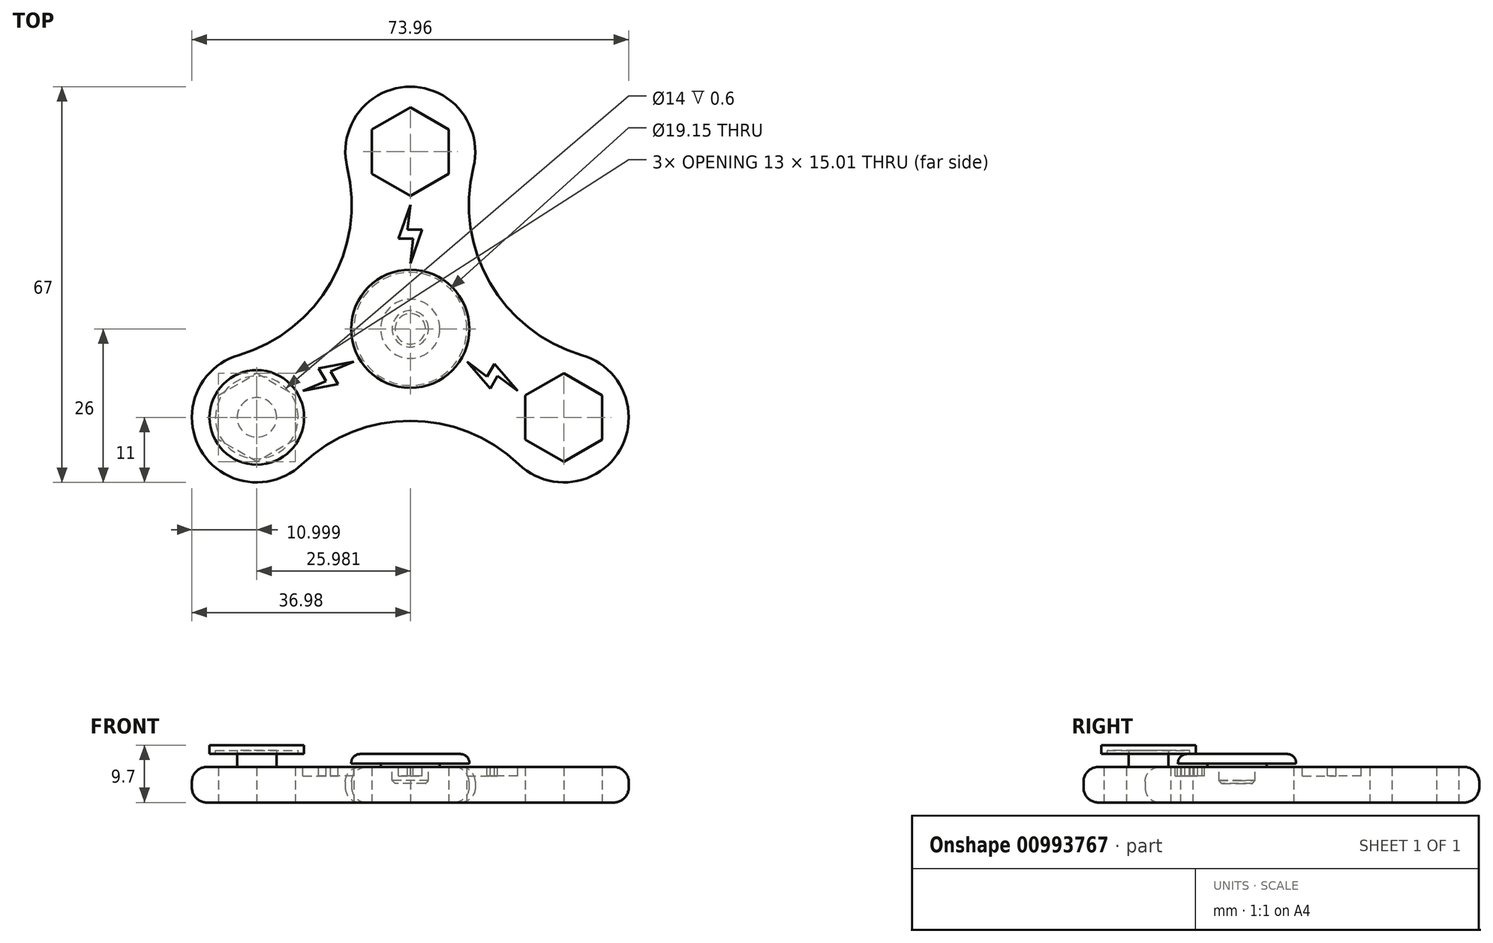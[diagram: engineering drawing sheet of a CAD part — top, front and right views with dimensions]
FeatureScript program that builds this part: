
annotation { "Feature Type Name" : "Feature", "Feature Type Description" : "" }
export const myFeature = defineFeature(function(context is Context, id is Id, definition is map)
    precondition{}
    {
        {
            var Q0;
            Q0=qCreatedBy(makeId("Top.planeOp"),FACE);
            var sketch = newSketch(context, id + "F0", { "sketchPlane" : qUnion([Q0])});
            skCircle(sketch, "E0", {"center": v(0, 0) * mm, "radius": 9.57 * mm});
            skLineSegment(sketch, "E1", {"start": v(0, 0) * mm, "end": v(0, 30) * mm, "construction": true});
            skLineSegment(sketch, "E2", {"start": v(0, 0) * mm, "end": v(25.98, -15) * mm, "construction": true});
            skLineSegment(sketch, "E3", {"start": v(0, 0) * mm, "end": v(-25.98, -15) * mm, "construction": true});
            skCircle(sketch, "E4", {"center": v(0, 0) * mm, "radius": 15.58 * mm, "construction": true});
            skArc(sketch, "E5", {"start": v(10.69, 27.39) * mm, "mid": v(0, 41) * mm, "end": v(-10.69, 27.39) * mm});
            skArc(sketch, "E6", {"start": v(18.38, -22.95) * mm, "mid": v(35.5, -20.5) * mm, "end": v(29.06, -4.44) * mm});
            skArc(sketch, "E7", {"start": v(-29.06, -4.44) * mm, "mid": v(-35.5, -20.5) * mm, "end": v(-18.38, -22.95) * mm});
            skArc(sketch, "E8", {"start": v(-29.06, -4.44) * mm, "mid": v(-13.49, 7.79) * mm, "end": v(-10.69, 27.39) * mm});
            skArc(sketch, "E9", {"start": v(10.69, 27.39) * mm, "mid": v(13.49, 7.79) * mm, "end": v(29.06, -4.44) * mm});
            skArc(sketch, "E10", {"start": v(18.38, -22.95) * mm, "mid": v(0, -15.57) * mm, "end": v(-18.38, -22.95) * mm});
            skCircle(sketch, "E11.cCircle", {"center": v(-25.98, -15) * mm, "radius": 6.5 * mm, "construction": true});
            skLineSegment(sketch, "E11.0", {"start": v(-19.48, -18.75) * mm, "end": v(-25.98, -22.5) * mm});
            skLineSegment(sketch, "E11.1", {"start": v(-25.98, -22.5) * mm, "end": v(-32.48, -18.75) * mm});
            skLineSegment(sketch, "E11.2", {"start": v(-32.48, -18.75) * mm, "end": v(-32.48, -11.25) * mm});
            skLineSegment(sketch, "E11.3", {"start": v(-32.48, -11.25) * mm, "end": v(-25.98, -7.5) * mm});
            skLineSegment(sketch, "E11.4", {"start": v(-25.98, -7.5) * mm, "end": v(-19.48, -11.25) * mm});
            skLineSegment(sketch, "E11.5", {"start": v(-19.48, -11.25) * mm, "end": v(-19.48, -18.75) * mm});
            skPoint(sketch, "E11.0.midPoint", {"position": v(-22.73, -20.63) * mm});
            skCircle(sketch, "E12.cCircle", {"center": v(25.98, -15) * mm, "radius": 6.5 * mm, "construction": true});
            skLineSegment(sketch, "E12.0", {"start": v(32.48, -18.75) * mm, "end": v(25.98, -22.5) * mm});
            skLineSegment(sketch, "E12.1", {"start": v(25.98, -22.5) * mm, "end": v(19.48, -18.75) * mm});
            skLineSegment(sketch, "E12.2", {"start": v(19.48, -18.75) * mm, "end": v(19.48, -11.25) * mm});
            skLineSegment(sketch, "E12.3", {"start": v(19.48, -11.25) * mm, "end": v(25.98, -7.5) * mm});
            skLineSegment(sketch, "E12.4", {"start": v(25.98, -7.5) * mm, "end": v(32.48, -11.25) * mm});
            skLineSegment(sketch, "E12.5", {"start": v(32.48, -11.25) * mm, "end": v(32.48, -18.75) * mm});
            skPoint(sketch, "E12.0.midPoint", {"position": v(29.23, -20.63) * mm});
            skCircle(sketch, "E13.cCircle", {"center": v(0, 30) * mm, "radius": 6.5 * mm, "construction": true});
            skLineSegment(sketch, "E13.0", {"start": v(-6.5, 33.75) * mm, "end": v(0, 37.5) * mm});
            skLineSegment(sketch, "E13.1", {"start": v(0, 37.5) * mm, "end": v(6.5, 33.75) * mm});
            skLineSegment(sketch, "E13.2", {"start": v(6.5, 33.75) * mm, "end": v(6.5, 26.25) * mm});
            skLineSegment(sketch, "E13.3", {"start": v(6.5, 26.25) * mm, "end": v(0, 22.5) * mm});
            skLineSegment(sketch, "E13.4", {"start": v(0, 22.5) * mm, "end": v(-6.5, 26.25) * mm});
            skLineSegment(sketch, "E13.5", {"start": v(-6.5, 26.25) * mm, "end": v(-6.5, 33.75) * mm});
            skPoint(sketch, "E13.0.midPoint", {"position": v(-3.25, 35.63) * mm});
            skSolve(sketch);
        }
        {
            var Q0;
            Q0 = qSketchRegion(id + "F0", true);
            extrude(context, id + "F1", {"entities" : qUnion([Q0]), "depth" : 6 * mm, "offsetDistance" : 25 * mm});
        }
        {
            var Q0;
            Q0=makeQuery(id+"F1.opExtrude","CAP_EDGE",EDGE,{"disambiguationData":[OSD([sQuery(id+"F0.wireOp",EDGE,"E8")])],"isStart":false});
            var Q1;
            Q1=makeQuery(id+"F1.opExtrude","CAP_EDGE",EDGE,{"disambiguationData":[OSD([sQuery(id+"F0.wireOp",EDGE,"E10")])],"isStart":true});
            fillet(context, id + "F2", {"entities" : qUnion([Q0, Q1]), "radius" : 2.5 * mm, "tangentPropagation" : true, "allowEdgeOverflow" : false});
        }
        {
            var Q0;
            Q0=makeQuery(id+"F1.opExtrude","CAP_FACE",FACE,{"disambiguationData":[OSD([sQuery(id+"F0.wireOp",EDGE,"E0"),sQuery(id+"F0.wireOp",EDGE,"E5"),sQuery(id+"F0.wireOp",EDGE,"E6"),sQuery(id+"F0.wireOp",EDGE,"E7"),sQuery(id+"F0.wireOp",EDGE,"E8"),sQuery(id+"F0.wireOp",EDGE,"E9"),sQuery(id+"F0.wireOp",EDGE,"E10"),sQuery(id+"F0.wireOp",EDGE,"E11.0"),sQuery(id+"F0.wireOp",EDGE,"E11.1"),sQuery(id+"F0.wireOp",EDGE,"E11.2"),sQuery(id+"F0.wireOp",EDGE,"E11.3"),sQuery(id+"F0.wireOp",EDGE,"E11.4"),sQuery(id+"F0.wireOp",EDGE,"E11.5"),sQuery(id+"F0.wireOp",EDGE,"E12.0"),sQuery(id+"F0.wireOp",EDGE,"E12.1"),sQuery(id+"F0.wireOp",EDGE,"E12.2"),sQuery(id+"F0.wireOp",EDGE,"E12.3"),sQuery(id+"F0.wireOp",EDGE,"E12.4"),sQuery(id+"F0.wireOp",EDGE,"E12.5"),sQuery(id+"F0.wireOp",EDGE,"E13.0"),sQuery(id+"F0.wireOp",EDGE,"E13.1"),sQuery(id+"F0.wireOp",EDGE,"E13.2"),sQuery(id+"F0.wireOp",EDGE,"E13.3"),sQuery(id+"F0.wireOp",EDGE,"E13.4"),sQuery(id+"F0.wireOp",EDGE,"E13.5")])],"isStart":false});
            var sketch = newSketch(context, id + "F3", { "sketchPlane" : qUnion([Q0])});
            skLineSegment(sketch, "E14", {"start": v(0, 21) * mm, "end": v(-2, 15.28) * mm});
            skLineSegment(sketch, "E15", {"start": v(0, 22.5) * mm, "end": v(0, 9.57) * mm, "construction": true});
            skLineSegment(sketch, "E16", {"start": v(-2, 15.28) * mm, "end": v(0.5, 15.28) * mm});
            skLineSegment(sketch, "E17", {"start": v(0, 11.07) * mm, "end": v(2, 16.78) * mm});
            skLineSegment(sketch, "E18", {"start": v(2, 16.78) * mm, "end": v(-0.5, 16.78) * mm});
            skLineSegment(sketch, "E19", {"start": v(0, 21) * mm, "end": v(-0.5, 16.78) * mm});
            skLineSegment(sketch, "E20", {"start": v(0, 11.07) * mm, "end": v(0.5, 15.28) * mm});
            skLineSegment(sketch, "E21.1.0", {"start": v(-18.18, -10.5) * mm, "end": v(-12.24, -9.37) * mm});
            skLineSegment(sketch, "E21.1.1", {"start": v(-18.18, -10.5) * mm, "end": v(-14.29, -8.83) * mm});
            skLineSegment(sketch, "E21.1.2", {"start": v(-15.54, -6.66) * mm, "end": v(-14.29, -8.83) * mm});
            skLineSegment(sketch, "E21.1.3", {"start": v(-9.6, -5.54) * mm, "end": v(-15.54, -6.66) * mm});
            skLineSegment(sketch, "E21.1.4", {"start": v(-9.6, -5.54) * mm, "end": v(-13.49, -7.2) * mm});
            skLineSegment(sketch, "E21.1.5", {"start": v(-12.24, -9.37) * mm, "end": v(-13.49, -7.2) * mm});
            skLineSegment(sketch, "E21.2.0", {"start": v(18.18, -10.5) * mm, "end": v(14.24, -5.91) * mm});
            skLineSegment(sketch, "E21.2.1", {"start": v(18.18, -10.5) * mm, "end": v(14.79, -7.96) * mm});
            skLineSegment(sketch, "E21.2.2", {"start": v(13.54, -10.12) * mm, "end": v(14.79, -7.96) * mm});
            skLineSegment(sketch, "E21.2.3", {"start": v(9.6, -5.54) * mm, "end": v(13.54, -10.12) * mm});
            skLineSegment(sketch, "E21.2.4", {"start": v(9.6, -5.54) * mm, "end": v(12.99, -8.08) * mm});
            skLineSegment(sketch, "E21.2.5", {"start": v(14.24, -5.91) * mm, "end": v(12.99, -8.08) * mm});
            skPoint(sketch, "E21.center", {"position": v(0, 0) * mm});
            skSolve(sketch);
        }
        {
            var Q0;
            Q0 = qSketchRegion(id + "F3", true);
            extrude(context, id + "F4", {"entities" : qUnion([Q0]), "operationType" : NewBodyOperationType.REMOVE, "oppositeDirection" : true, "depth" : 1.5 * mm, "offsetDistance" : 25 * mm});
        }
        {
            var Q0;
            Q0=makeQuery(id+"F1.opExtrude","CAP_FACE",FACE,{"disambiguationData":[OSD([sQuery(id+"F0.wireOp",EDGE,"E0"),sQuery(id+"F0.wireOp",EDGE,"E5"),sQuery(id+"F0.wireOp",EDGE,"E6"),sQuery(id+"F0.wireOp",EDGE,"E7"),sQuery(id+"F0.wireOp",EDGE,"E8"),sQuery(id+"F0.wireOp",EDGE,"E9"),sQuery(id+"F0.wireOp",EDGE,"E10"),sQuery(id+"F0.wireOp",EDGE,"E11.0"),sQuery(id+"F0.wireOp",EDGE,"E11.1"),sQuery(id+"F0.wireOp",EDGE,"E11.2"),sQuery(id+"F0.wireOp",EDGE,"E11.3"),sQuery(id+"F0.wireOp",EDGE,"E11.4"),sQuery(id+"F0.wireOp",EDGE,"E11.5"),sQuery(id+"F0.wireOp",EDGE,"E12.0"),sQuery(id+"F0.wireOp",EDGE,"E12.1"),sQuery(id+"F0.wireOp",EDGE,"E12.2"),sQuery(id+"F0.wireOp",EDGE,"E12.3"),sQuery(id+"F0.wireOp",EDGE,"E12.4"),sQuery(id+"F0.wireOp",EDGE,"E12.5"),sQuery(id+"F0.wireOp",EDGE,"E13.0"),sQuery(id+"F0.wireOp",EDGE,"E13.1"),sQuery(id+"F0.wireOp",EDGE,"E13.2"),sQuery(id+"F0.wireOp",EDGE,"E13.3"),sQuery(id+"F0.wireOp",EDGE,"E13.4"),sQuery(id+"F0.wireOp",EDGE,"E13.5")])],"isStart":false});
            var sketch = newSketch(context, id + "F5", { "sketchPlane" : qUnion([Q0])});
            skCircle(sketch, "E22", {"center": v(0, 0) * mm, "radius": 3.07 * mm});
            skSolve(sketch);
        }
        {
            var Q0;
            Q0 = qSketchRegion(id + "F5", true);
            extrude(context, id + "F6", {"entities" : qUnion([Q0]), "oppositeDirection" : true, "depth" : 2.8 * mm, "offsetDistance" : 25 * mm});
        }
        {
            var Q0;
            Q0=makeQuery(id+"F6.opExtrude","CAP_FACE",FACE,{"disambiguationData":[OSD([sQuery(id+"F5.wireOp",EDGE,"E22")])],"isStart":true});
            var sketch = newSketch(context, id + "F7", { "sketchPlane" : qUnion([Q0])});
            skCircle(sketch, "E23", {"center": v(0, 0) * mm, "radius": 5 * mm});
            skSolve(sketch);
        }
        {
            var Q0;
            Q0 = qSketchRegion(id + "F7", true);
            extrude(context, id + "F8", {"entities" : qUnion([Q0]), "operationType" : NewBodyOperationType.ADD, "depth" : .6 * mm, "offsetDistance" : 25 * mm});
        }
        {
            var Q0;
            Q0=makeQuery(id+"F8.opExtrude","CAP_FACE",FACE,{"disambiguationData":[OSD([sQuery(id+"F7.wireOp",EDGE,"E23")])],"isStart":false});
            var sketch = newSketch(context, id + "F9", { "sketchPlane" : qUnion([Q0])});
            skCircle(sketch, "E24", {"center": v(0, 0) * mm, "radius": 10 * mm});
            skSolve(sketch);
        }
        {
            var Q0;
            Q0 = qSketchRegion(id + "F9", true);
            extrude(context, id + "F10", {"entities" : qUnion([Q0]), "operationType" : NewBodyOperationType.ADD, "depth" : 1.6 * mm, "offsetDistance" : 25 * mm});
        }
        {
            var Q0;
            Q0=makeQuery(id+"F10.opExtrude","CAP_EDGE",EDGE,{"disambiguationData":[OSD([sQuery(id+"F9.wireOp",EDGE,"E24")])],"isStart":false});
            fillet(context, id + "F11", {"entities" : qUnion([Q0]), "radius" : 1.5 * mm, "tangentPropagation" : true, "allowEdgeOverflow" : false});
        }
        {
            var Q0;
            Q0=makeQuery(id+"F6.opExtrude","CAP_EDGE",EDGE,{"disambiguationData":[OSD([sQuery(id+"F5.wireOp",EDGE,"E22")])],"isStart":false});
            chamfer(context, id + "F12", {"entities" : qUnion([Q0]), "width" : .5 * mm, "tangentPropagation" : true});
        }
        {
            var Q0;
            Q0=makeQuery(id+"F1.opExtrude","CAP_FACE",FACE,{"disambiguationData":[OSD([sQuery(id+"F0.wireOp",EDGE,"E0"),sQuery(id+"F0.wireOp",EDGE,"E5"),sQuery(id+"F0.wireOp",EDGE,"E6"),sQuery(id+"F0.wireOp",EDGE,"E7"),sQuery(id+"F0.wireOp",EDGE,"E8"),sQuery(id+"F0.wireOp",EDGE,"E9"),sQuery(id+"F0.wireOp",EDGE,"E10"),sQuery(id+"F0.wireOp",EDGE,"E11.0"),sQuery(id+"F0.wireOp",EDGE,"E11.1"),sQuery(id+"F0.wireOp",EDGE,"E11.2"),sQuery(id+"F0.wireOp",EDGE,"E11.3"),sQuery(id+"F0.wireOp",EDGE,"E11.4"),sQuery(id+"F0.wireOp",EDGE,"E11.5"),sQuery(id+"F0.wireOp",EDGE,"E12.0"),sQuery(id+"F0.wireOp",EDGE,"E12.1"),sQuery(id+"F0.wireOp",EDGE,"E12.2"),sQuery(id+"F0.wireOp",EDGE,"E12.3"),sQuery(id+"F0.wireOp",EDGE,"E12.4"),sQuery(id+"F0.wireOp",EDGE,"E12.5"),sQuery(id+"F0.wireOp",EDGE,"E13.0"),sQuery(id+"F0.wireOp",EDGE,"E13.1"),sQuery(id+"F0.wireOp",EDGE,"E13.2"),sQuery(id+"F0.wireOp",EDGE,"E13.3"),sQuery(id+"F0.wireOp",EDGE,"E13.4"),sQuery(id+"F0.wireOp",EDGE,"E13.5")])],"isStart":false});
            var sketch = newSketch(context, id + "F13", { "sketchPlane" : qUnion([Q0])});
            skCircle(sketch, "E25", {"center": v(-25.98, -15) * mm, "radius": 3.35 * mm});
            skSolve(sketch);
        }
        {
            var Q0;
            Q0 = qSketchRegion(id + "F13", true);
            extrude(context, id + "F14", {"entities" : qUnion([Q0]), "depth" : 2.8 * mm, "offsetDistance" : 25 * mm});
        }
        {
            var Q0;
            Q0=makeQuery(id+"F14.opExtrude","CAP_FACE",FACE,{"disambiguationData":[OSD([sQuery(id+"F13.wireOp",EDGE,"E25")])],"isStart":false});
            var sketch = newSketch(context, id + "F15", { "sketchPlane" : qUnion([Q0])});
            skCircle(sketch, "E26", {"center": v(-25.98, -15) * mm, "radius": 8 * mm});
            skSolve(sketch);
        }
        {
            var Q0;
            Q0 = qSketchRegion(id + "F15", true);
            extrude(context, id + "F16", {"entities" : qUnion([Q0]), "operationType" : NewBodyOperationType.ADD, "depth" : .9 * mm, "offsetDistance" : 25 * mm});
        }
        {
            var Q0;
            Q0=makeQuery(id+"F16.opExtrude","CAP_FACE",FACE,{"disambiguationData":[OSD([sQuery(id+"F15.wireOp",EDGE,"E26")])],"isStart":true});
            var sketch = newSketch(context, id + "F17", { "sketchPlane" : qUnion([Q0])});
            skCircle(sketch, "E27.0", {"center": v(-25.98, 15) * mm, "radius": 7 * mm});
            skSolve(sketch);
        }
        {
            var Q0;
            Q0=makeQuery(id+"F17.imprint","IMPRINT",FACE,{"disambiguationData":[TD([[makeQuery(id+"F17.imprint","IMPRINT",EDGE,{"derivedFrom":sQuery(id+"F17.wireOp",EDGE,"E27.0")}),-1.0]])]});
            extrude(context, id + "F18", {"entities" : qUnion([Q0]), "operationType" : NewBodyOperationType.ADD, "depth" : .6 * mm, "offsetDistance" : 25 * mm});
        }
    });
